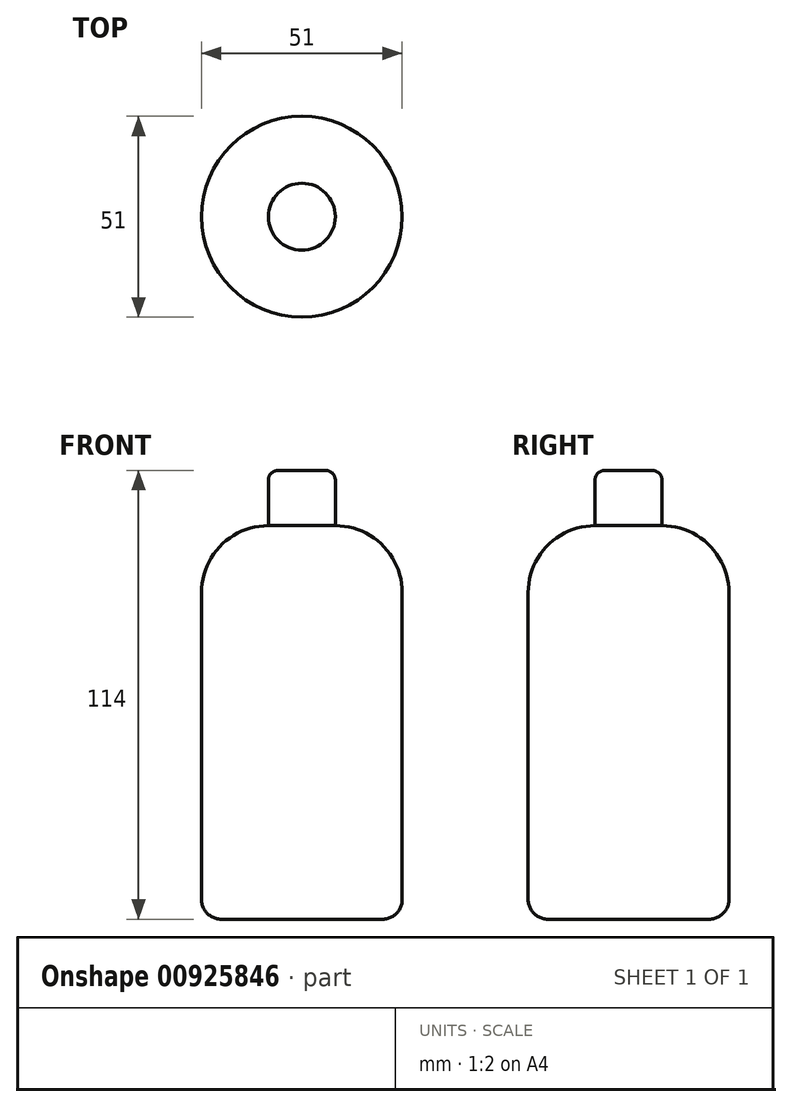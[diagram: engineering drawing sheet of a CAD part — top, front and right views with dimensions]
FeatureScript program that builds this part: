
annotation { "Feature Type Name" : "Feature", "Feature Type Description" : "" }
export const myFeature = defineFeature(function(context is Context, id is Id, definition is map)
    precondition{}
    {
        {
            var Q0;
            Q0=qCreatedBy(makeId("Front.planeOp"),FACE);
            var sketch = newSketch(context, id + "F0", { "sketchPlane" : qUnion([Q0])});
            skLineSegment(sketch, "E0", {"start": v(0, 0) * mm, "end": v(25.5, 0) * mm});
            skLineSegment(sketch, "E1", {"start": v(25.5, 0) * mm, "end": v(25.5, 83) * mm});
            skLineSegment(sketch, "E2", {"start": v(8.5, 100) * mm, "end": v(0, 100) * mm});
            skLineSegment(sketch, "E3", {"start": v(0, 100) * mm, "end": v(0, 0) * mm});
            skPoint(sketch, "E4.visualSharp", {"position": v(25.5, 100) * mm});
            skArc(sketch, "E4.filletArc", {"start": v(25.5, 83) * mm, "mid": v(20.52, 95.02) * mm, "end": v(8.5, 100) * mm});
            skSolve(sketch);
        }
        {
            var Q0;
            Q0=makeQuery(id+"F0.imprint","IMPRINT",FACE,{"disambiguationData":[TD([[makeQuery(id+"F0.imprint","IMPRINT",EDGE,{"derivedFrom":sQuery(id+"F0.wireOp",EDGE,"E0")}),1.0]])]});
            var Q1;
            Q1=sQuery(id+"F0.wireOp",EDGE,"E3");
            revolve(context, id + "F1", {"surfaceOperationType" : NewSurfaceOperationType.NEW, "entities" : qUnion([Q0]), "axis" : qUnion([Q1]), "revolveType" : RevolveType.FULL});
        }
        {
            var Q0;
            Q0=makeQuery(id+"F1.opRevolve","SWEPT_FACE",FACE,{"disambiguationData":[OSD([sQuery(id+"F0.wireOp",EDGE,"E2")])]});
            var sketch = newSketch(context, id + "F2", { "sketchPlane" : qUnion([Q0])});
            skCircle(sketch, "E5.0", {"center": v(0, 0) * mm, "radius": 8.5 * mm});
            skSolve(sketch);
        }
        {
            var Q0;
            Q0=qSketchRegion(id+"F2",true);
            extrude(context, id + "F3", {"entities" : qUnion([Q0]), "operationType" : NewBodyOperationType.ADD, "depth" : 14 * mm, "offsetDistance" : 25 * mm});
        }
        {
            var Q0;
            Q0=makeQuery(id+"F3.opExtrude","CAP_EDGE",EDGE,{"disambiguationData":[OSD([sQuery(id+"F2.wireOp",EDGE,"E5.0")])],"isStart":false});
            fillet(context, id + "F4", {"entities" : qUnion([Q0]), "radius" : 2.4 * mm, "tangentPropagation" : true, "allowEdgeOverflow" : false});
        }
        {
            var Q0;
            Q0=makeQuery(id+"F1.opRevolve","SWEPT_EDGE",EDGE,{"disambiguationData":[OSD([sQuery(id+"F0.wireOp",EDGE,"E0"),sQuery(id+"F0.wireOp",EDGE,"E1")])]});
            fillet(context, id + "F5", {"entities" : qUnion([Q0]), "radius" : 5 * mm, "tangentPropagation" : true, "allowEdgeOverflow" : false});
        }
    });
